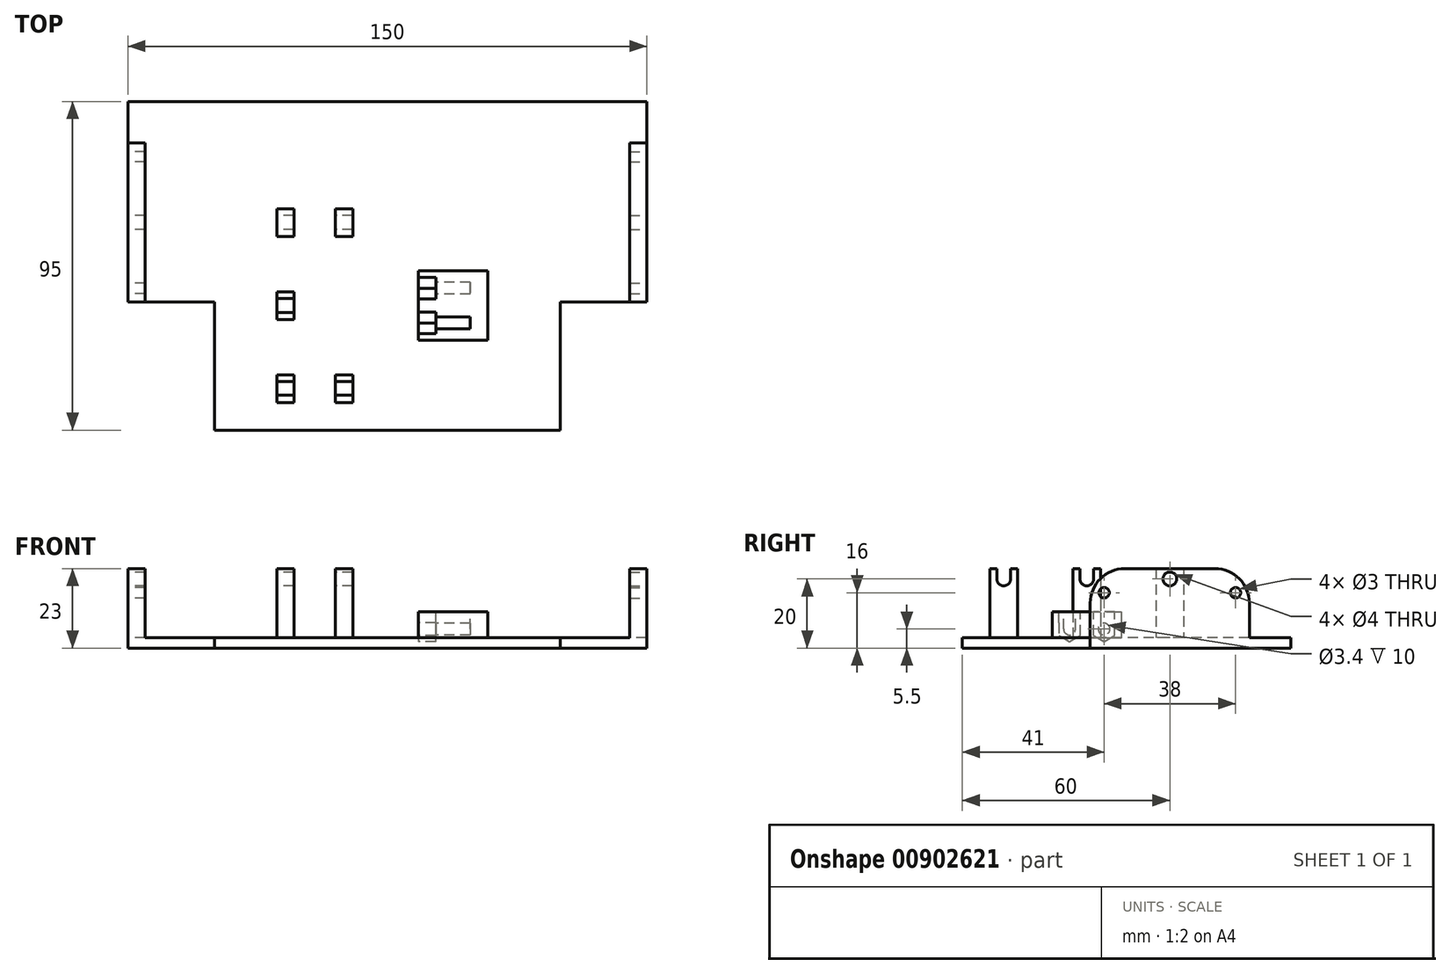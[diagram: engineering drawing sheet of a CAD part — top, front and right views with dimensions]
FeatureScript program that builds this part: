
annotation { "Feature Type Name" : "Feature", "Feature Type Description" : "" }
export const myFeature = defineFeature(function(context is Context, id is Id, definition is map)
    precondition{}
    {
        {
            var Q0;
            Q0=qCreatedBy(makeId("Top.planeOp"),FACE);
            var sketch = newSketch(context, id + "F0", { "sketchPlane" : qUnion([Q0])});
            skLineSegment(sketch, "E0.top", {"start": v(50, -18.5) * mm, "end": v(-50, -18.5) * mm});
            skLineSegment(sketch, "E0.left", {"start": v(50, 18.5) * mm, "end": v(50, -18.5) * mm});
            skLineSegment(sketch, "E0.right", {"start": v(-50, 18.5) * mm, "end": v(-50, -18.5) * mm});
            skPoint(sketch, "E0.middle", {"position": v(0, 0) * mm});
            skLineSegment(sketch, "E1.bottom", {"start": v(-75, 76.5) * mm, "end": v(75, 76.5) * mm});
            skLineSegment(sketch, "E1.top", {"start": v(-75, 18.5) * mm, "end": v(-50, 18.5) * mm});
            skLineSegment(sketch, "E1.left", {"start": v(-75, 76.5) * mm, "end": v(-75, 18.5) * mm});
            skLineSegment(sketch, "E1.right", {"start": v(75, 76.5) * mm, "end": v(75, 18.5) * mm});
            skLineSegment(sketch, "E2.trimOffspring", {"start": v(50, 18.5) * mm, "end": v(75, 18.5) * mm});
            skSolve(sketch);
        }
        {
            var Q0;
            Q0=qSketchRegion(id+"F0",true);
            extrude(context, id + "F1", {"entities" : qUnion([Q0]), "oppositeDirection" : true, "depth" : 3 * mm, "offsetDistance" : 25.4 * mm});
        }
        {
            var Q0;
            Q0=makeQuery(id+"F1.opExtrude","SWEPT_FACE",FACE,{"disambiguationData":[OSD([sQuery(id+"F0.wireOp",EDGE,"E1.right")])]});
            var sketch = newSketch(context, id + "F2", { "sketchPlane" : qUnion([Q0])});
            skLineSegment(sketch, "E3.bottom", {"start": v(18.5, -3) * mm, "end": v(64.5, -3) * mm});
            skLineSegment(sketch, "E3.top", {"start": v(28.5, 20) * mm, "end": v(54.5, 20) * mm});
            skLineSegment(sketch, "E3.left", {"start": v(18.5, -3) * mm, "end": v(18.5, 10) * mm});
            skLineSegment(sketch, "E3.right", {"start": v(64.5, -3) * mm, "end": v(64.5, 10) * mm});
            skCircle(sketch, "E4", {"center": v(41.5, 17) * mm, "radius": 2 * mm});
            skCircle(sketch, "E5", {"center": v(22.5, 13) * mm, "radius": 1.5 * mm});
            skCircle(sketch, "E6", {"center": v(60.5, 13) * mm, "radius": 1.5 * mm});
            skPoint(sketch, "E7.visualSharp", {"position": v(18.5, 20) * mm});
            skArc(sketch, "E7.filletArc", {"start": v(28.5, 20) * mm, "mid": v(21.43, 17.07) * mm, "end": v(18.5, 10) * mm});
            skPoint(sketch, "E8.visualSharp", {"position": v(64.5, 20) * mm});
            skArc(sketch, "E8.filletArc", {"start": v(64.5, 10) * mm, "mid": v(61.57, 17.07) * mm, "end": v(54.5, 20) * mm});
            skSolve(sketch);
        }
        {
            var Q0;
            Q0=qSketchRegion(id+"F2",true);
            extrude(context, id + "F3", {"entities" : qUnion([Q0]), "operationType" : NewBodyOperationType.ADD, "oppositeDirection" : true, "depth" : 5 * mm, "offsetDistance" : 25.4 * mm});
        }
        {
            var Q0;
            Q0=makeQuery(id+"F1.opExtrude","SWEPT_FACE",FACE,{"disambiguationData":[OSD([sQuery(id+"F0.wireOp",EDGE,"E1.left")])]});
            var sketch = newSketch(context, id + "F4", { "sketchPlane" : qUnion([Q0])});
            skLineSegment(sketch, "E9.0.0", {"start": v(-64.5, 0) * mm, "end": v(-18.5, 0) * mm});
            skLineSegment(sketch, "E9.0.1", {"start": v(-18.5, 0) * mm, "end": v(-18.5, 10) * mm});
            skArc(sketch, "E9.0.2", {"start": v(-18.5, 10) * mm, "mid": v(-21.43, 17.07) * mm, "end": v(-28.5, 20) * mm});
            skLineSegment(sketch, "E9.0.3", {"start": v(-28.5, 20) * mm, "end": v(-54.5, 20) * mm});
            skArc(sketch, "E9.0.4", {"start": v(-54.5, 20) * mm, "mid": v(-61.57, 17.07) * mm, "end": v(-64.5, 10) * mm});
            skLineSegment(sketch, "E9.0.5", {"start": v(-64.5, 10) * mm, "end": v(-64.5, 0) * mm});
            skCircle(sketch, "E10.0", {"center": v(-60.5, 13) * mm, "radius": 1.5 * mm});
            skCircle(sketch, "E11.0", {"center": v(-41.5, 17) * mm, "radius": 2 * mm});
            skCircle(sketch, "E12.0", {"center": v(-22.5, 13) * mm, "radius": 1.5 * mm});
            skSolve(sketch);
        }
        {
            var Q0;
            Q0=qSketchRegion(id+"F4",true);
            extrude(context, id + "F5", {"entities" : qUnion([Q0]), "operationType" : NewBodyOperationType.ADD, "oppositeDirection" : true, "depth" : 5 * mm, "offsetDistance" : 25.4 * mm});
        }
        {
            var Q0;
            Q0=makeQuery(id+"F1.opExtrude","CAP_FACE",FACE,{"disambiguationData":[OSD([sQuery(id+"F0.wireOp",EDGE,"E0.top"),sQuery(id+"F0.wireOp",EDGE,"E0.left"),sQuery(id+"F0.wireOp",EDGE,"E0.right"),sQuery(id+"F0.wireOp",EDGE,"E1.bottom"),sQuery(id+"F0.wireOp",EDGE,"E1.top"),sQuery(id+"F0.wireOp",EDGE,"E1.left"),sQuery(id+"F0.wireOp",EDGE,"E1.right"),sQuery(id+"F0.wireOp",EDGE,"E2.trimOffspring")])],"isStart":true});
            var sketch = newSketch(context, id + "F6", { "sketchPlane" : qUnion([Q0])});
            skLineSegment(sketch, "E13.bottom", {"start": v(-32, 45.5) * mm, "end": v(-27, 45.5) * mm});
            skLineSegment(sketch, "E13.top", {"start": v(-32, 37.5) * mm, "end": v(-27, 37.5) * mm});
            skLineSegment(sketch, "E13.left", {"start": v(-32, 45.5) * mm, "end": v(-32, 37.5) * mm});
            skLineSegment(sketch, "E13.right", {"start": v(-27, 45.5) * mm, "end": v(-27, 37.5) * mm});
            skLineSegment(sketch, "E14.bottom", {"start": v(-32, 21.5) * mm, "end": v(-27, 21.5) * mm});
            skLineSegment(sketch, "E14.top", {"start": v(-32, 13.5) * mm, "end": v(-27, 13.5) * mm});
            skLineSegment(sketch, "E14.left", {"start": v(-32, 21.5) * mm, "end": v(-32, 13.5) * mm});
            skLineSegment(sketch, "E14.right", {"start": v(-27, 21.5) * mm, "end": v(-27, 13.5) * mm});
            skLineSegment(sketch, "E15.bottom", {"start": v(-32, -2.5) * mm, "end": v(-27, -2.5) * mm});
            skLineSegment(sketch, "E15.top", {"start": v(-32, -10.5) * mm, "end": v(-27, -10.5) * mm});
            skLineSegment(sketch, "E15.left", {"start": v(-32, -2.5) * mm, "end": v(-32, -10.5) * mm});
            skLineSegment(sketch, "E15.right", {"start": v(-27, -2.5) * mm, "end": v(-27, -10.5) * mm});
            skLineSegment(sketch, "E16.bottom", {"start": v(-15, 45.5) * mm, "end": v(-10, 45.5) * mm});
            skLineSegment(sketch, "E16.top", {"start": v(-15, 37.5) * mm, "end": v(-10, 37.5) * mm});
            skLineSegment(sketch, "E16.left", {"start": v(-15, 45.5) * mm, "end": v(-15, 37.5) * mm});
            skLineSegment(sketch, "E16.right", {"start": v(-10, 45.5) * mm, "end": v(-10, 37.5) * mm});
            skLineSegment(sketch, "E17.bottom", {"start": v(-15, -2.5) * mm, "end": v(-10, -2.5) * mm});
            skLineSegment(sketch, "E17.top", {"start": v(-15, -10.5) * mm, "end": v(-10, -10.5) * mm});
            skLineSegment(sketch, "E17.left", {"start": v(-15, -2.5) * mm, "end": v(-15, -10.5) * mm});
            skLineSegment(sketch, "E17.right", {"start": v(-10, -2.5) * mm, "end": v(-10, -10.5) * mm});
            skSolve(sketch);
        }
        {
            var Q0;
            Q0=qSketchRegion(id+"F6",true);
            extrude(context, id + "F7", {"entities" : qUnion([Q0]), "operationType" : NewBodyOperationType.ADD, "depth" : 20 * mm, "offsetDistance" : 25.4 * mm});
        }
        {
            var Q0;
            Q0=makeQuery(id+"F7.opExtrude","SWEPT_FACE",FACE,{"disambiguationData":[OSD([sQuery(id+"F6.wireOp",EDGE,"E15.left")])]});
            var sketch = newSketch(context, id + "F8", { "sketchPlane" : qUnion([Q0])});
            skArc(sketch, "E18", {"start": v(4.5, 17) * mm, "mid": v(6.53, 15) * mm, "end": v(8.5, 17.05) * mm});
            skArc(sketch, "E19", {"start": v(-19.5, 17) * mm, "mid": v(-17.5, 15) * mm, "end": v(-15.5, 17) * mm});
            skLineSegment(sketch, "E20", {"start": v(-19.5, 17) * mm, "end": v(-19.5, 20.1) * mm});
            skLineSegment(sketch, "E21", {"start": v(-15.5, 17) * mm, "end": v(-15.5, 20.64) * mm});
            skLineSegment(sketch, "E22", {"start": v(-15.5, 20.64) * mm, "end": v(-19.5, 20.1) * mm});
            skLineSegment(sketch, "E23", {"start": v(4.5, 17) * mm, "end": v(4.48, 22.22) * mm});
            skLineSegment(sketch, "E24", {"start": v(8.5, 17.05) * mm, "end": v(8.37, 22.14) * mm});
            skLineSegment(sketch, "E25", {"start": v(8.37, 22.14) * mm, "end": v(4.48, 22.22) * mm});
            skSolve(sketch);
        }
        {
            var Q0;
            Q0=qSketchRegion(id+"F8",true);
            extrude(context, id + "F9", {"entities" : qUnion([Q0]), "operationType" : NewBodyOperationType.REMOVE, "oppositeDirection" : true, "depth" : 25.4 * mm, "offsetDistance" : 25.4 * mm});
        }
        {
            var Q0;
            Q0=makeQuery(id+"F7.opExtrude","SWEPT_FACE",FACE,{"disambiguationData":[OSD([sQuery(id+"F6.wireOp",EDGE,"E13.left")])]});
            var sketch = newSketch(context, id + "F10", { "sketchPlane" : qUnion([Q0])});
            skCircle(sketch, "E26.0", {"center": v(-41.5, 17) * mm, "radius": 2 * mm});
            skSolve(sketch);
        }
        {
            var Q0;
            Q0=qSketchRegion(id+"F10",true);
            extrude(context, id + "F11", {"entities" : qUnion([Q0]), "operationType" : NewBodyOperationType.REMOVE, "oppositeDirection" : true, "depth" : 25.4 * mm, "offsetDistance" : 25.4 * mm});
        }
        {
            var Q0;
            Q0=makeQuery(id+"F1.opExtrude","CAP_FACE",FACE,{"disambiguationData":[OSD([sQuery(id+"F0.wireOp",EDGE,"E0.top"),sQuery(id+"F0.wireOp",EDGE,"E0.left"),sQuery(id+"F0.wireOp",EDGE,"E0.right"),sQuery(id+"F0.wireOp",EDGE,"E1.bottom"),sQuery(id+"F0.wireOp",EDGE,"E1.top"),sQuery(id+"F0.wireOp",EDGE,"E1.left"),sQuery(id+"F0.wireOp",EDGE,"E1.right"),sQuery(id+"F0.wireOp",EDGE,"E2.trimOffspring")])],"isStart":true});
            var sketch = newSketch(context, id + "F12", { "sketchPlane" : qUnion([Q0])});
            skLineSegment(sketch, "E27.bottom", {"start": v(9, 7.5) * mm, "end": v(29, 7.5) * mm});
            skLineSegment(sketch, "E27.top", {"start": v(9, 27.5) * mm, "end": v(29, 27.5) * mm});
            skLineSegment(sketch, "E27.left", {"start": v(9, 7.5) * mm, "end": v(9, 27.5) * mm});
            skLineSegment(sketch, "E27.right", {"start": v(29, 7.5) * mm, "end": v(29, 27.5) * mm});
            skSolve(sketch);
        }
        {
            var Q0;
            Q0=makeQuery(id+"F12.imprint","IMPRINT",FACE,{"disambiguationData":[TD([[makeQuery(id+"F12.imprint","IMPRINT",EDGE,{"derivedFrom":sQuery(id+"F12.wireOp",EDGE,"E27.bottom")}),1.0]])]});
            extrude(context, id + "F13", {"entities" : qUnion([Q0]), "operationType" : NewBodyOperationType.ADD, "depth" : 7.5 * mm, "offsetDistance" : 25 * mm});
        }
        {
            var Q0;
            Q0=makeQuery(id+"F13.opExtrude","SWEPT_FACE",FACE,{"disambiguationData":[OSD([sQuery(id+"F12.wireOp",EDGE,"E27.left")])]});
            var sketch = newSketch(context, id + "F14", { "sketchPlane" : qUnion([Q0])});
            skCircle(sketch, "E28.cCircle", {"center": v(-22.5, 2.5) * mm, "radius": 3.1 * mm, "construction": true});
            skLineSegment(sketch, "E28.0", {"start": v(-19.4, 0.71) * mm, "end": v(-22.5, -1.08) * mm});
            skLineSegment(sketch, "E28.1", {"start": v(-22.5, -1.08) * mm, "end": v(-25.6, 0.71) * mm});
            skLineSegment(sketch, "E28.2", {"start": v(-25.6, 0.71) * mm, "end": v(-25.6, 4.29) * mm});
            skLineSegment(sketch, "E28.3", {"start": v(-25.6, 4.29) * mm, "end": v(-22.5, 6.08) * mm});
            skLineSegment(sketch, "E28.4", {"start": v(-22.5, 6.08) * mm, "end": v(-19.4, 4.29) * mm});
            skLineSegment(sketch, "E28.5", {"start": v(-19.4, 4.29) * mm, "end": v(-19.4, 0.71) * mm});
            skPoint(sketch, "E28.0.midPoint", {"position": v(-20.95, -0.18) * mm});
            skCircle(sketch, "E29.cCircle", {"center": v(-12.5, 2.5) * mm, "radius": 3.1 * mm, "construction": true});
            skPoint(sketch, "E29.cCircle.centerSnap0", {"position": v(-25.6, 2.5) * mm});
            skLineSegment(sketch, "E29.0", {"start": v(-9.4, 0.71) * mm, "end": v(-12.5, -1.08) * mm});
            skLineSegment(sketch, "E29.1", {"start": v(-12.5, -1.08) * mm, "end": v(-15.6, 0.71) * mm});
            skLineSegment(sketch, "E29.2", {"start": v(-15.6, 0.71) * mm, "end": v(-15.6, 4.29) * mm});
            skLineSegment(sketch, "E29.3", {"start": v(-15.6, 4.29) * mm, "end": v(-12.5, 6.08) * mm});
            skLineSegment(sketch, "E29.4", {"start": v(-12.5, 6.08) * mm, "end": v(-9.4, 4.29) * mm});
            skLineSegment(sketch, "E29.5", {"start": v(-9.4, 4.29) * mm, "end": v(-9.4, 0.71) * mm});
            skPoint(sketch, "E29.0.midPoint", {"position": v(-10.95, -0.18) * mm});
            skLineSegment(sketch, "E30", {"start": v(-17.5, -2.38) * mm, "end": v(-17.5, 12.1) * mm, "construction": true});
            skCircle(sketch, "E31", {"center": v(-22.5, 2.5) * mm, "radius": 1.7 * mm});
            skCircle(sketch, "E32", {"center": v(-12.5, 2.5) * mm, "radius": 1.7 * mm});
            skLineSegment(sketch, "E33.bottom", {"start": v(-25.6, 4.29) * mm, "end": v(-19.4, 4.29) * mm});
            skLineSegment(sketch, "E33.top", {"start": v(-25.6, 10.64) * mm, "end": v(-19.4, 10.64) * mm});
            skLineSegment(sketch, "E33.left", {"start": v(-25.6, 4.29) * mm, "end": v(-25.6, 10.64) * mm});
            skLineSegment(sketch, "E33.right", {"start": v(-19.4, 4.29) * mm, "end": v(-19.4, 10.64) * mm});
            skLineSegment(sketch, "E34.bottom", {"start": v(-15.6, 4.29) * mm, "end": v(-9.38, 4.29) * mm});
            skLineSegment(sketch, "E34.top", {"start": v(-15.6, 11.52) * mm, "end": v(-9.38, 11.52) * mm});
            skLineSegment(sketch, "E34.left", {"start": v(-15.6, 4.29) * mm, "end": v(-15.6, 11.52) * mm});
            skLineSegment(sketch, "E35", {"start": v(-9.38, 4.29) * mm, "end": v(-9.38, 11.52) * mm});
            skSolve(sketch);
        }
        {
            var Q0;
            Q0=qSketchRegion(id+"F14",true);
            var Q1;
            Q1=makeQuery(id+"F14.imprint","IMPRINT",FACE,{"disambiguationData":[TD([[makeQuery(id+"F14.imprint","IMPRINT",EDGE,{"derivedFrom":sQuery(id+"F14.wireOp",EDGE,"E31")}),1.0]])]});
            var Q2;
            Q2=makeQuery(id+"F14.imprint","IMPRINT",FACE,{"disambiguationData":[TD([[makeQuery(id+"F14.imprint","IMPRINT",EDGE,{"derivedFrom":sQuery(id+"F14.wireOp",EDGE,"E32")}),1.0]])]});
            extrude(context, id + "F15", {"entities" : qUnion([Q0, Q1, Q2]), "operationType" : NewBodyOperationType.REMOVE, "oppositeDirection" : true, "depth" : 5 * mm, "offsetDistance" : 25 * mm});
        }
        {
            var Q0;
            Q0=makeQuery(id+"F14.imprint","IMPRINT",FACE,{"disambiguationData":[TD([[makeQuery(id+"F14.imprint","IMPRINT",EDGE,{"derivedFrom":sQuery(id+"F14.wireOp",EDGE,"E31")}),1.0]])]});
            var Q1;
            Q1=makeQuery(id+"F14.imprint","IMPRINT",FACE,{"disambiguationData":[TD([[makeQuery(id+"F14.imprint","IMPRINT",EDGE,{"derivedFrom":sQuery(id+"F14.wireOp",EDGE,"E32")}),1.0]])]});
            extrude(context, id + "F16", {"entities" : qUnion([Q0, Q1]), "operationType" : NewBodyOperationType.REMOVE, "oppositeDirection" : true, "depth" : 15 * mm, "offsetDistance" : 25 * mm});
        }
        {
            var Q0;
            Q0=makeQuery(id+"F15.boolean.opBoolean","COPY",FACE,{"derivedFrom":makeQuery(id+"F15.opExtrude","CAP_FACE",FACE,{"disambiguationData":[OSD([sQuery(id+"F14.wireOp",EDGE,"E29.0"),sQuery(id+"F14.wireOp",EDGE,"E29.1"),sQuery(id+"F14.wireOp",EDGE,"E29.2"),sQuery(id+"F14.wireOp",EDGE,"E29.5"),sQuery(id+"F14.wireOp",EDGE,"E34.bottom"),sQuery(id+"F14.wireOp",EDGE,"E34.top"),sQuery(id+"F14.wireOp",EDGE,"E34.left"),sQuery(id+"F14.wireOp",EDGE,"E35")])],"isStart":false})});
            var sketch = newSketch(context, id + "F17", { "sketchPlane" : qUnion([Q0])});
            skLineSegment(sketch, "E36.bottom", {"start": v(-14.2, 2.5) * mm, "end": v(-10.8, 2.5) * mm});
            skLineSegment(sketch, "E36.top", {"start": v(-14.2, 8.48) * mm, "end": v(-10.8, 8.48) * mm});
            skLineSegment(sketch, "E36.left", {"start": v(-14.2, 2.5) * mm, "end": v(-14.2, 8.48) * mm});
            skLineSegment(sketch, "E36.right", {"start": v(-10.8, 2.5) * mm, "end": v(-10.8, 8.48) * mm});
            skSolve(sketch);
        }
        {
            var Q0;
            {var subQ0=sQuery(id+"F17.wireOp",EDGE,"E36.left");var subQ1=sQuery(id+"F17.wireOp",EDGE,"E36.bottom");var subQ2=makeQuery(id+"F15.opExtrude","CAP_FACE",FACE,{"disambiguationData":[OSD([sQuery(id+"F14.wireOp",EDGE,"E29.0"),sQuery(id+"F14.wireOp",EDGE,"E29.1"),sQuery(id+"F14.wireOp",EDGE,"E29.2"),sQuery(id+"F14.wireOp",EDGE,"E29.5"),sQuery(id+"F14.wireOp",EDGE,"E34.bottom"),sQuery(id+"F14.wireOp",EDGE,"E34.top"),sQuery(id+"F14.wireOp",EDGE,"E34.left"),sQuery(id+"F14.wireOp",EDGE,"E35")])],"isStart":false});var subQ3=makeQuery(id+"F16.boolean.opBoolean","INTERSECT",EDGE,{"derivedFrom":[makeQuery(id+"F15.boolean.opBoolean","COPY",FACE,{"derivedFrom":subQ2}),makeQuery(id+"F16.opExtrude","SWEPT_FACE",FACE,{"disambiguationData":[OSD([sQuery(id+"F14.wireOp",EDGE,"E32")])]})]});var subQ4=makeQuery(id+"F17.imprint","INTERSECT",VERTEX,{"derivedFrom":[subQ3,subQ1,subQ0]});Q0=makeQuery(id+"F17.imprint","IMPRINT",FACE,{"disambiguationData":[TD([[makeQuery(id+"F17.imprint","IMPRINT",EDGE,{"disambiguationData":[TD([[subQ4,-1.0]])],"derivedFrom":subQ0}),-1.0]])]});}
            extrude(context, id + "F18", {"entities" : qUnion([Q0]), "operationType" : NewBodyOperationType.REMOVE, "oppositeDirection" : true, "depth" : 10 * mm, "offsetDistance" : 25 * mm});
        }
    });
